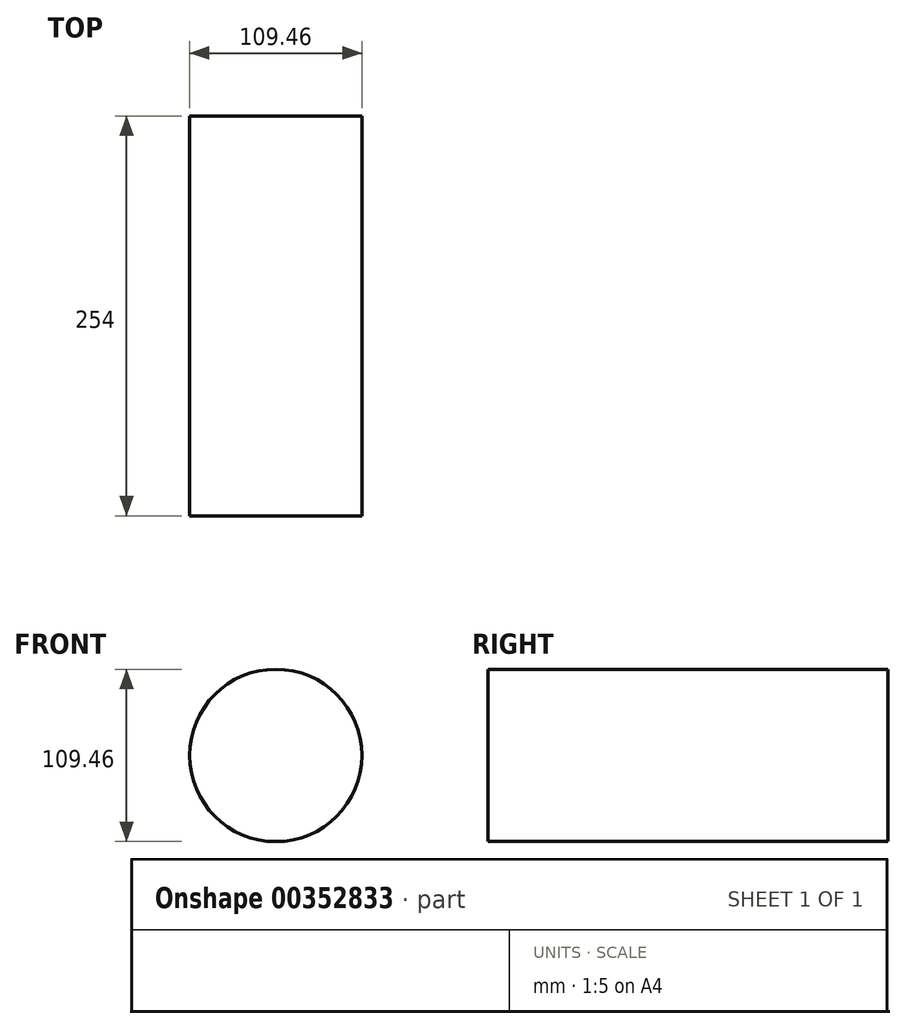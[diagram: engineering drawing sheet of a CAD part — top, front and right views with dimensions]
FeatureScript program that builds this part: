
annotation { "Feature Type Name" : "Feature", "Feature Type Description" : "" }
export const myFeature = defineFeature(function(context is Context, id is Id, definition is map)
    precondition{}
    {
        {
            var Q0;
            Q0=qCreatedBy(makeId("Front.planeOp"),FACE);
            var sketch = newSketch(context, id + "F0", { "sketchPlane" : qUnion([Q0])});
            skCircle(sketch, "E0", {"center": v(0, 0) * mm, "radius": 54.73 * mm});
            skSolve(sketch);
        }
        {
            var Q0;
            Q0=makeQuery(id+"F0.imprint","IMPRINT",FACE,{"disambiguationData":[TD([[makeQuery(id+"F0.imprint","IMPRINT",EDGE,{"derivedFrom":sQuery(id+"F0.wireOp",EDGE,"E0")}),1.0]])]});
            extrude(context, id + "F1", {"entities" : qUnion([Q0]), "depth" : 254 * mm});
        }
    });
